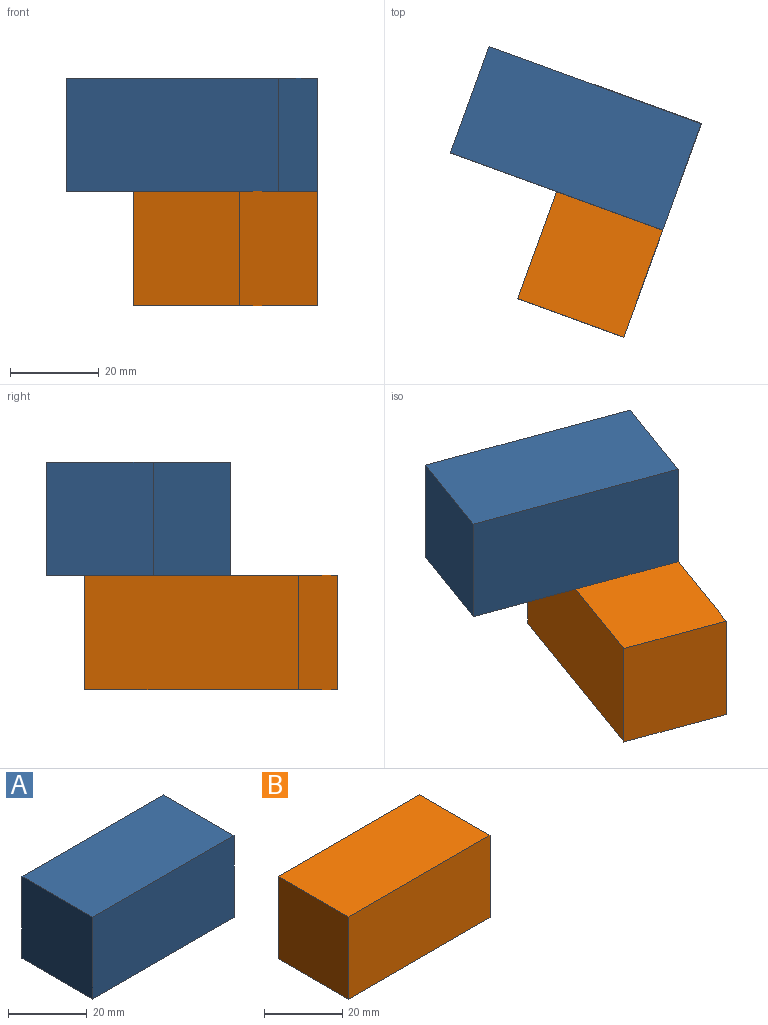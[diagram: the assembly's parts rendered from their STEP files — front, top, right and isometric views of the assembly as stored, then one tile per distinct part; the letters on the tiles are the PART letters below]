
ASSEMBLY  parts=2 mates=1
PART A: 6 faces, bbox 50.8x25.4x25.5 mm
  f0: plane 50.78x25.4mm, normal (0,0,1), area 1289.9mm2, adj f1,f3,f4,f5
  f1: plane 25.47x25.4mm, normal (-1,0,0), area 646.9mm2, adj f0,f2,f4,f5
  f2: plane 50.78x25.4mm, normal (0,0,-1), area 1289.9mm2, adj f1,f3,f4,f5
  f3: plane 25.47x25.4mm, normal (1,0,0), area 646.9mm2, adj f0,f2,f4,f5
  f4: plane 50.78x25.47mm, normal (0,-1,0), area 1293.3mm2, adj f0,f1,f2,f3
  f5: plane 50.78x25.47mm, normal (0,1,0), area 1293.3mm2, adj f0,f1,f2,f3
PART B: 6 faces, bbox 51.1x25.4x25.7 mm
  f0: plane 51.14x25.4mm, normal (0,0,1), area 1298.9mm2, adj f1,f3,f4,f5
  f1: plane 25.72x25.4mm, normal (-1,0,0), area 653.3mm2, adj f0,f2,f4,f5
  f2: plane 51.14x25.4mm, normal (0,0,-1), area 1298.9mm2, adj f1,f3,f4,f5
  f3: plane 25.72x25.4mm, normal (1,0,0), area 653.3mm2, adj f0,f2,f4,f5
  f4: plane 51.14x25.72mm, normal (0,-1,0), area 1315.3mm2, adj f0,f1,f2,f3
  f5: plane 51.14x25.72mm, normal (0,1,0), area 1315.3mm2, adj f0,f1,f2,f3
PLACE A rot(axis=(0,0,-1),20deg) t=(70.75,-56.76,19.45)mm
PLACE B rot(axis=(0,0,1),70deg) t=(-7.73,70.53,25.89)mm
MATE fastened B.f0 <-> A.f2  axis (0,0,1) through (-36.21,-44.86,7.93)mm
